# Revit family: Shower-Column-Bradley_Corp-COL-4C-Type_H_Drain
name_source: partatom
category: Plumbing Fixtures
revit_build: Autodesk Revit MEP 2012 (Build: 20110309_2315(x64)
units: mm (PartAtom-declared; Revit-internal decimal feet)

## types (44) — shared parameters
ADA Compliant = No
Assembly Code = D2010710
Buy American Act = To Be Determined
Cold Water Connection Diameter = 1"
Cold Water Connection Radius = 0"
Column Material = Metal - Bradley Corp - Stainless Steel - Satin
Depth = 12.338 "
Description = 4-Person Column Shower
Drain Diameter = 3"
Drain Radius = 2"
Height = 78.25 "
Hot Water Connection Diameter = 1"
Hot Water Connection Radius = 0"
Manufacturer = Bradley Corporation
MasterFormat Number = 22 42 23
MasterFormat Title = Commercial Showers
Maximum Operating Pressure = 0.00 psi
Minimum Flow = 0 GPM
OmniClass Table 21 Number = 21-04 20 10 60
OmniClass Table 21 Title = Plumbing Fixtures
OmniClass Table 23 Number = 23-31 17 00
OmniClass Table 23 Title = Showers
Product Tech Data URL - English = http://bradleycorp.com
Showerhead Material = Metal - Bradley Corp - Chrome
Specifications URL = http://www.bradleycorp.com
URL = http://www.bradleycorp.com
Valve Material = Metal - Bradley Corp - Chrome
Vent Diameter = 2"
Vent Radius = 1"
Version = 2.0
Width = 12.338 "
zero-valued in all types: CWFU, HWFU, Percentage of Recycled Content, WFU

## per-type parameters (varying)
| type | Air Metering Valve | CALC_ASTT | CALC_EqPlate | CALC_EqTMV | Deluxe Showerhead with Ball Joint | Economy Soft Flow Showerhead with Ball Joint | Equa-Flo HD Pressure Balancing Valve | Equa-Flo Pressure Balancing Valve | Hot and Cold Compression Valve | Model | Optional 1.5 GPM Flow Control | SVHC | Severe Service Showerhead | Single Compression Valve | Standard Showerhead | Thermostatic Mixing Valve | TouchTime Metering Valve | Type Comments |
| Hot Tempered and Cold Supplies | No | No | No | No | No | No | No | No | No | - | No | No | No | No | No | No | No | - |
| COL-4C-EF-S | No | No | Yes | No | No | No | No | Yes | No | COL-4C | No | No | No | No | Yes | No | No | 4-Person Column Shower with Equa-Flo Pressure Balancing Valve and Standard Showerhead |
| COL-4C-EF-S-G | No | No | Yes | No | No | No | No | Yes | No | COL-4C | Yes | No | No | No | Yes | No | No | 4-Person Column Shower with Equa-Flo Pressure Balancing Valve and Standard Showerhead with optional 1.5GPM Flow Control |
| COL-4C-HD-S | No | No | Yes | Yes | No | No | Yes | No | No | COL-4C | No | No | No | No | Yes | No | No | 4-Person Column Shower with Equa-Flo HD Pressure Balancing Valve and Standard Showerhead |
| COL-4C-HD-S-G | No | No | Yes | Yes | No | No | Yes | No | No | COL-4C | Yes | No | No | No | Yes | No | No | 4-Person Column Shower with Equa-Flo HD Pressure Balancing Valve and Standard Showerhead with optional 1.5GPM Flow Control |
| COL-4C-TMV-S | No | No | Yes | Yes | No | No | No | No | No | COL-4C | No | No | No | No | Yes | Yes | No | 4-Person Column Shower with Thermostatic Mixing Valve and Standard Showerhead |
| COL-4C-TMV-S-G | No | No | Yes | Yes | No | No | No | No | No | COL-4C | Yes | No | No | No | Yes | Yes | No | 4-Person Column Shower with Thermostatic Mixing Valve and Standard Showerhead with optional 1.5GPM Flow Control |
| COL-4C-HC-S-G | No | No | No | No | No | No | No | No | Yes | COL-4C | No | Yes | No | No | Yes | No | No | 4-Person Column Shower with Hot and Cold Compression Valve and Standard Showerhead |
| COL-4C-HC-S | No | No | No | No | No | No | No | No | Yes | COL-4C | Yes | Yes | No | No | Yes | No | No | 4-Person Column Shower with Hot and Cold Compression Valve and Standard Showerhead with optional 1.5GPM Flow Control |
| COL-4C-EF-SX | No | No | Yes | No | No | No | No | Yes | No | COL-4C | No | No | Yes | No | No | No | No | 4-Person Column Shower with Equa-Flo Pressure Balancing Valve and Severe Service Showerhead |
| COL-4C-EF-SX-G | No | No | Yes | No | No | No | No | Yes | No | COL-4C | Yes | No | Yes | No | No | No | No | 4-Person Column Shower with Equa-Flo Pressure Balancing Valve and Severe Service Showerhead with optional 1.5GPM Flow Control |
| COL-4C-HD-SX | No | No | Yes | Yes | No | No | Yes | No | No | COL-4C | No | No | Yes | No | No | No | No | 4-Person Column Shower with Equa-Flo HD Pressure Balancing Valve and Severe Service Showerhead |
| COL-4C-HD-SX-G | No | No | Yes | Yes | No | No | Yes | No | No | COL-4C | Yes | No | Yes | No | No | No | No | 4-Person Column Shower with Equa-Flo HD Pressure Balancing Valve and Severe Service Showerhead with optional 1.5GPM Flow Control |
| COL-4C-TMV-SX | No | No | Yes | Yes | No | No | No | No | No | COL-4C | No | No | Yes | No | No | Yes | No | 4-Person Column Shower with Thermostatic Mixing Valve and Severe Service Showerhead |
| COL-4C-TMV-SX-G | No | No | Yes | Yes | No | No | No | No | No | COL-4C | Yes | No | Yes | No | No | Yes | No | 4-Person Column Shower with Thermostatic Mixing Valve and Severe Service Showerhead with optional 1.5GPM Flow Control |
| COL-4C-HC-SX-G | No | No | No | No | No | No | No | No | Yes | COL-4C | No | Yes | Yes | No | No | No | No | 4-Person Column Shower with Hot and Cold Compression Valve and Severe Service Showerhead |
| COL-4C-HC-SX | No | No | No | No | No | No | No | No | Yes | COL-4C | Yes | Yes | Yes | No | No | No | No | 4-Person Column Shower with Hot and Cold Compression Valve and Severe Service Showerhead with optional 1.5GPM Flow Control |
| COL-4C-EF-SF | No | No | Yes | No | Yes | No | No | Yes | No | COL-4C | No | No | No | No | No | No | No | 4-Person Column Shower with Equa-Flo Pressure Balancing Valve and Deluxe Showerhead with Ball Joint |
| COL-4C-HD-SF | No | No | Yes | Yes | Yes | No | Yes | No | No | COL-4C | No | No | No | No | No | No | No | 4-Person Column Shower with Equa-Flo HD Pressure Balancing Valve and Deluxe Showerhead with Ball Joint |
| COL-4C-TMV-SF | No | No | Yes | Yes | Yes | No | No | No | No | COL-4C | No | No | No | No | No | Yes | No | 4-Person Column Shower with Thermostatic Mixing Valve and Deluxe Showerhead with Ball Joint |
| COL-4C-HC-SF | No | No | No | No | Yes | No | No | No | Yes | COL-4C | No | Yes | No | No | No | No | No | 4-Person Column Shower with Hot and Cold Compression Valve and Deluxe Showerhead with Ball Joint |
| COL-4C-EF-ES | No | No | Yes | No | No | Yes | No | Yes | No | COL-4C | No | No | No | No | No | No | No | 4-Person Column Shower with Equa-Flo Pressure Balancing Valve and Economy Soft Flow Showerhead with Ball Joint |
| COL-4C-HD-ES | No | No | Yes | Yes | No | Yes | Yes | No | No | COL-4C | No | No | No | No | No | No | No | 4-Person Column Shower with Equa-Flo HD Pressure Balancing Valve and Economy Soft Flow Showerhead with Ball Joint |
| COL-4C-TMV-ES | No | No | Yes | Yes | No | Yes | No | No | No | COL-4C | No | No | No | No | No | Yes | No | 4-Person Column Shower with Thermostatic Mixing Valve and Economy Soft Flow Showerhead with Ball Joint |
| COL-4C-HC-ES | No | No | No | No | No | Yes | No | No | Yes | COL-4C | No | Yes | No | No | No | No | No | 4-Person Column Shower with Hot and Cold Compression Valve and Economy Soft Flow Showerhead with Ball Joint |
| Single Tempered/Cold Supply | No | No | No | No | No | No | No | No | No | - | No | No | No | No | No | No | No | - |
| COL-4C-AST-S | Yes | Yes | No | No | No | No | No | No | No | COL-4C | No | No | No | No | Yes | No | No | 4-Person Column Shower with Air Metering Valve and Standard Showerhead |
| COL-4C-AST-S-G | Yes | Yes | No | No | No | No | No | No | No | COL-4C | Yes | No | No | No | Yes | No | No | 4-Person Column Shower with Air Metering Valve and Standard Showerhead with optional 1.5GPM Flow Control |
| COL-4C-AST-SX | Yes | Yes | No | No | No | No | No | No | No | COL-4C | No | No | Yes | No | No | No | No | 4-Person Column Shower with Air Metering Valve and Severe Service Showerhead |
| COL-4C-AST-SX-G | Yes | Yes | No | No | No | No | No | No | No | COL-4C | Yes | No | Yes | No | No | No | No | 4-Person Column Shower with Air Metering Valve and Severe Service Showerhead with optional 1.5GPM Flow Control |
| COL-4C-AST-SF | Yes | Yes | No | No | Yes | No | No | No | No | COL-4C | No | No | No | No | No | No | No | 4-Person Column Shower with Air Metering Valve and Deluxe Showerhead with Ball Joint |
| COL-4C-AST-ES | Yes | Yes | No | No | No | Yes | No | No | No | COL-4C | No | No | No | No | No | No | No | 4-Person Column Shower with Air Metering Valve and Economy Soft Flow Showerhead with Ball Joint |
| COL-4C-SV-S | No | No | No | No | No | No | No | No | No | COL-4C | No | Yes | No | Yes | Yes | No | No | 4-Person Column Shower with Single Compression Valve and Standard Showerhead |
| COL-4C-SV-S-G | No | No | No | No | No | No | No | No | No | COL-4C | Yes | Yes | No | Yes | Yes | No | No | 4-Person Column Shower with Single Compression Valve and Standard Showerhead with optional 1.5GPM Flow Control |
| COL-4C-SV-SX | No | No | No | No | No | No | No | No | No | COL-4C | No | Yes | Yes | Yes | No | No | No | 4-Person Column Shower with Single Compression Valve and Severe Service Showerhead |
| COL-4C-SV-SX-G | No | No | No | No | No | No | No | No | No | COL-4C | Yes | Yes | Yes | Yes | No | No | No | 4-Person Column Shower with Single Compression Valve and Severe Service Showerhead with optional 1.5GPM Flow Control |
| COL-4C-SV-SF | No | No | No | No | Yes | No | No | No | No | COL-4C | No | Yes | No | Yes | No | No | No | 4-Person Column Shower with Single Compression Valve and Deluxe Showerhead with Ball Joint |
| COL-4C-SV-ES | No | No | No | No | No | Yes | No | No | No | COL-4C | No | Yes | No | Yes | No | No | No | 4-Person Column Shower with Single Compression Valve and Economy Soft Flow Showerhead with Ball Joint |
| COL-4C-TT-S | No | Yes | No | No | No | No | No | No | No | COL-4C | No | No | No | No | Yes | No | Yes | 4-Person Column Shower with TouchTime÷ Metering Valve and Standard Showerhead |
| COL-4C-TT-S-G | No | Yes | No | No | No | No | No | No | No | COL-4C | Yes | No | No | No | Yes | No | Yes | 4-Person Column Shower with TouchTime÷ Metering Valve and Standard Showerhead with optional 1.5GPM Flow Control |
| COL-4C-TT-SX | No | Yes | No | No | No | No | No | No | No | COL-4C | No | No | Yes | No | No | No | Yes | 4-Person Column Shower with TouchTime÷ Metering Valve and Severe Service Showerhead |
| COL-4C-TT-SX-G | No | Yes | No | No | No | No | No | No | No | COL-4C | Yes | No | Yes | No | No | No | Yes | 4-Person Column Shower with TouchTime÷ Metering Valve and Severe Service Showerhead with optional 1.5GPM Flow Control |
| COL-4C-TT-SF | No | Yes | No | No | Yes | No | No | No | No | COL-4C | No | No | No | No | No | No | Yes | 4-Person Column Shower with TouchTime÷ Metering Valve and Deluxe Showerhead with Ball Joint |
| COL-4C-TT-ES | No | Yes | No | No | No | Yes | No | No | No | COL-4C | No | No | No | No | No | No | Yes | 4-Person Column Shower with TouchTime÷ Metering Valve and Economy Soft Flow Showerhead wiht Ball Joint |

## geometry (parser evidence)
native form markers: Blend x4, Sweep x10
no freeform markers — native parametric forms only
